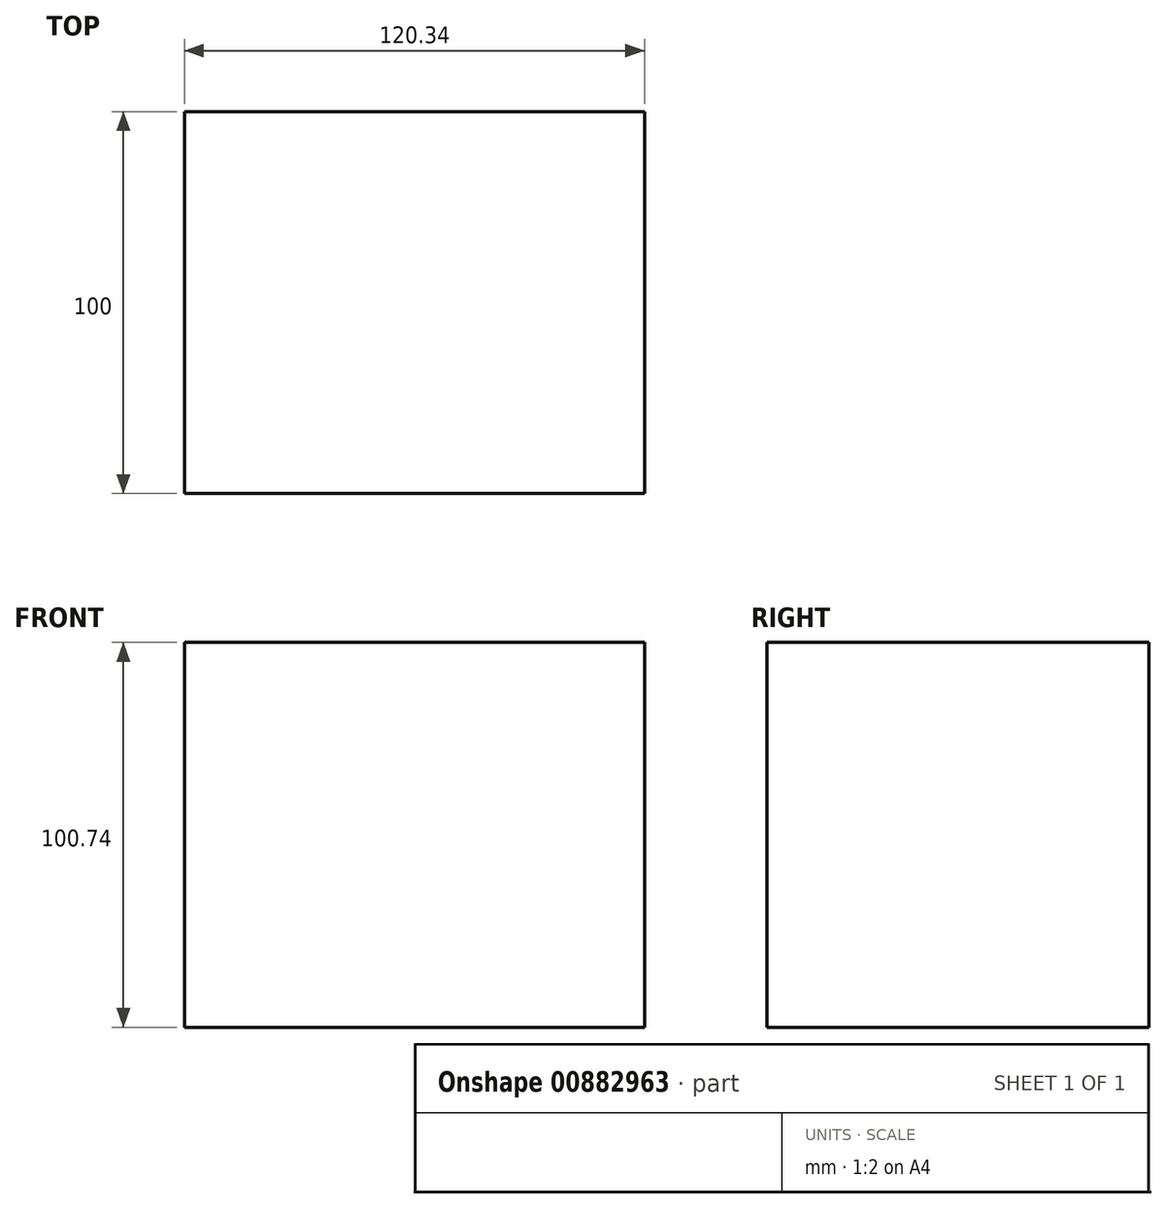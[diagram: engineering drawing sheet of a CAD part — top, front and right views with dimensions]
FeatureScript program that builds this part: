
annotation { "Feature Type Name" : "Feature", "Feature Type Description" : "" }
export const myFeature = defineFeature(function(context is Context, id is Id, definition is map)
    precondition{}
    {
        {
            var Q0;
            Q0=qCreatedBy(makeId("Front.planeOp"),FACE);
            var sketch = newSketch(context, id + "F0", { "sketchPlane" : qUnion([Q0])});
            skLineSegment(sketch, "E0.bottom", {"start": v(60.17, 50.37) * mm, "end": v(-60.17, 50.37) * mm});
            skLineSegment(sketch, "E0.top", {"start": v(60.17, -50.37) * mm, "end": v(-60.17, -50.37) * mm});
            skLineSegment(sketch, "E0.left", {"start": v(60.17, 50.37) * mm, "end": v(60.17, -50.37) * mm});
            skLineSegment(sketch, "E0.right", {"start": v(-60.17, 50.37) * mm, "end": v(-60.17, -50.37) * mm});
            skPoint(sketch, "E0.middle", {"position": v(0, 0) * mm});
            skSolve(sketch);
        }
        {
            var Q0;
            Q0=makeQuery(id+"F0.imprint","IMPRINT",FACE,{"disambiguationData":[TD([[makeQuery(id+"F0.imprint","IMPRINT",EDGE,{"derivedFrom":sQuery(id+"F0.wireOp",EDGE,"E0.bottom")}),1.0]])]});
            var sketch = newSketch(context, id + "F1", { "sketchPlane" : qUnion([Q0])});
            skLineSegment(sketch, "E1", {"start": v(-60.25, 50.15) * mm, "end": v(0, 0) * mm});
            skSolve(sketch);
        }
        {
            var Q0;
            Q0=makeQuery(id+"F1.imprint","IMPRINT",FACE,{"disambiguationData":[TD([[makeQuery(id+"F1.imprint","IMPRINT",EDGE,{"derivedFrom":makeQuery(id+"F0.imprint","IMPRINT",EDGE,{"derivedFrom":sQuery(id+"F0.wireOp",EDGE,"E0.bottom")})}),1.0]])]});
            extrude(context, id + "F2", {"entities" : qUnion([Q0]), "depth" : 25 * mm, "offsetDistance" : 25 * mm});
        }
        {
            var Q0;
            Q0=makeQuery(id+"F2.opExtrude","CAP_FACE",FACE,{"disambiguationData":[OSD([sQuery(id+"F0.wireOp",EDGE,"E0.bottom"),sQuery(id+"F0.wireOp",EDGE,"E0.top"),sQuery(id+"F0.wireOp",EDGE,"E0.left"),sQuery(id+"F0.wireOp",EDGE,"E0.right")])],"isStart":false});
            extrude(context, id + "F3", {"entities" : qUnion([Q0]), "operationType" : NewBodyOperationType.ADD, "depth" : 25 * mm, "offsetDistance" : 25 * mm});
        }
        {
            var Q0;
            Q0=makeQuery(id+"F3.opExtrude","CAP_FACE",FACE,{"disambiguationData":[OSD([sQuery(id+"F0.wireOp",EDGE,"E0.bottom"),sQuery(id+"F0.wireOp",EDGE,"E0.top"),sQuery(id+"F0.wireOp",EDGE,"E0.left"),sQuery(id+"F0.wireOp",EDGE,"E0.right")])],"isStart":false});
            extrude(context, id + "F4", {"entities" : qUnion([Q0]), "operationType" : NewBodyOperationType.ADD, "depth" : 50 * mm, "offsetDistance" : 25 * mm});
        }
    });
